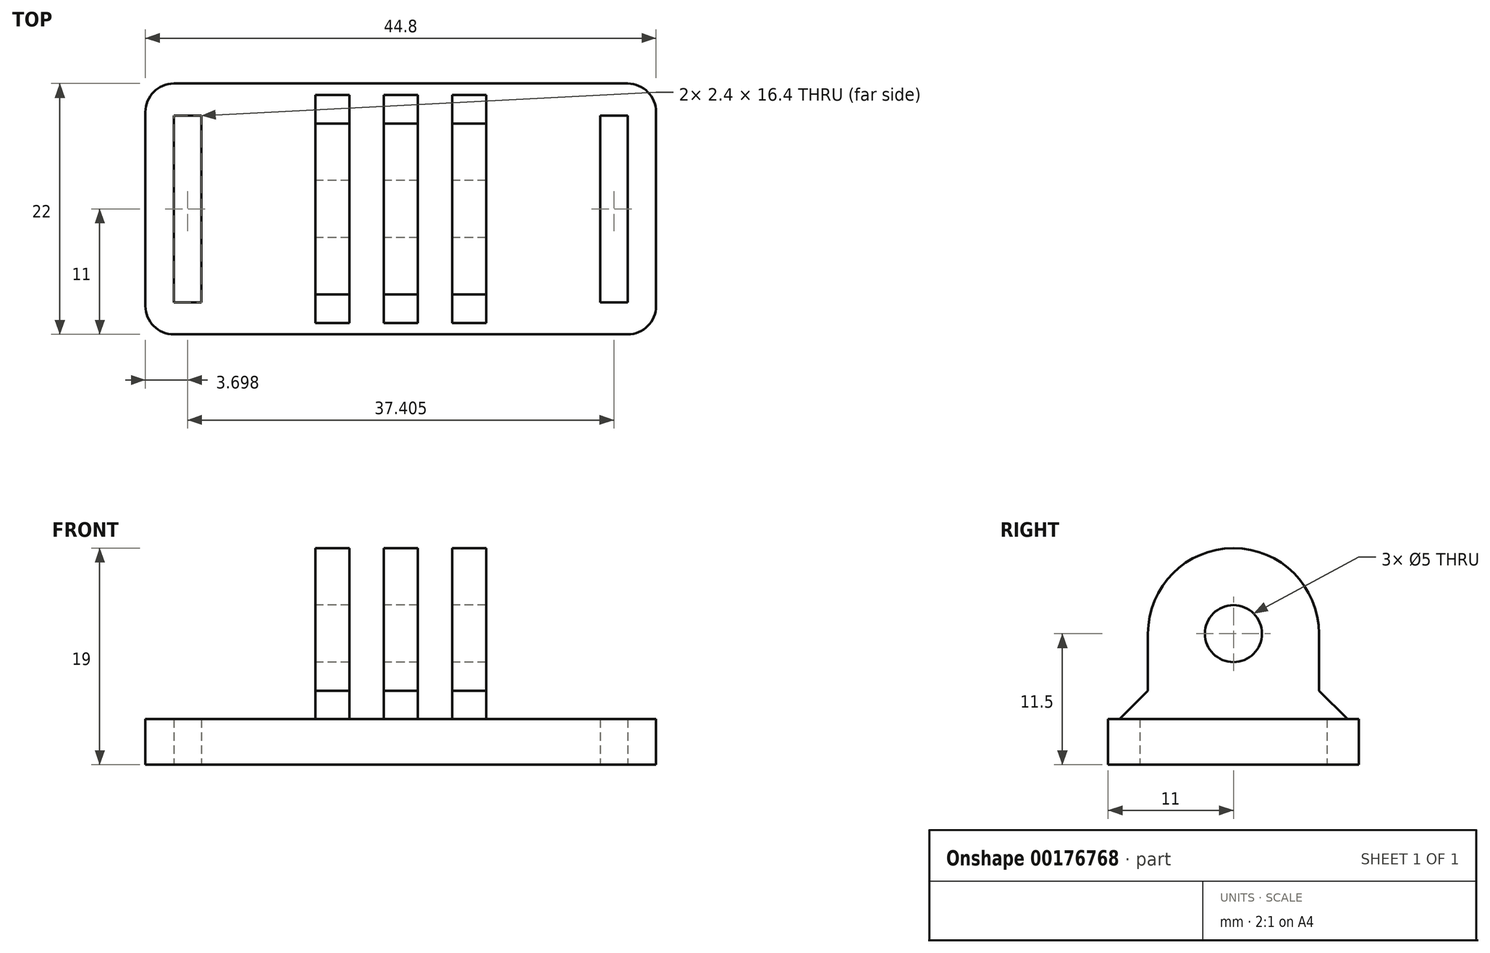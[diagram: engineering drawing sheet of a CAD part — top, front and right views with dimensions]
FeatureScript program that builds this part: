
annotation { "Feature Type Name" : "Feature", "Feature Type Description" : "" }
export const myFeature = defineFeature(function(context is Context, id is Id, definition is map)
    precondition{}
    {
        {
            var Q0;
            Q0=qCreatedBy(makeId("Top.planeOp"),FACE);
            var sketch = newSketch(context, id + "F0", { "sketchPlane" : qUnion([Q0])});
            skLineSegment(sketch, "E0.bottom", {"start": v(-22.4, 11) * mm, "end": v(22.4, 11) * mm});
            skLineSegment(sketch, "E0.top", {"start": v(-22.4, -11) * mm, "end": v(22.4, -11) * mm});
            skLineSegment(sketch, "E0.left", {"start": v(-22.4, 11) * mm, "end": v(-22.4, -11) * mm});
            skLineSegment(sketch, "E0.right", {"start": v(22.4, 11) * mm, "end": v(22.4, -11) * mm});
            skPoint(sketch, "E0.middle", {"position": v(0, 0) * mm});
            skLineSegment(sketch, "E1", {"start": v(5.64, 11) * mm, "end": v(0, 11) * mm});
            skLineSegment(sketch, "E2", {"start": v(0, 11) * mm, "end": v(-5.64, 11) * mm});
            skLineSegment(sketch, "E3.bottom", {"start": v(-7.5, 7.5) * mm, "end": v(-4.5, 7.5) * mm});
            skLineSegment(sketch, "E3.top", {"start": v(-7.5, -7.5) * mm, "end": v(-4.5, -7.5) * mm});
            skLineSegment(sketch, "E3.left", {"start": v(-7.5, 7.5) * mm, "end": v(-7.5, -7.5) * mm});
            skLineSegment(sketch, "E3.right", {"start": v(-4.5, 7.5) * mm, "end": v(-4.5, -7.5) * mm});
            skPoint(sketch, "E3.middle", {"position": v(-6, 0) * mm});
            skLineSegment(sketch, "E4.bottom", {"start": v(-1.5, 7.5) * mm, "end": v(1.5, 7.5) * mm});
            skLineSegment(sketch, "E4.top", {"start": v(-1.5, -7.5) * mm, "end": v(1.5, -7.5) * mm});
            skLineSegment(sketch, "E4.left", {"start": v(-1.5, 7.5) * mm, "end": v(-1.5, -7.5) * mm});
            skLineSegment(sketch, "E4.right", {"start": v(1.5, 7.5) * mm, "end": v(1.5, -7.5) * mm});
            skLineSegment(sketch, "E5.bottom", {"start": v(4.5, 7.5) * mm, "end": v(7.5, 7.5) * mm});
            skLineSegment(sketch, "E5.top", {"start": v(4.5, -7.5) * mm, "end": v(7.5, -7.5) * mm});
            skLineSegment(sketch, "E5.left", {"start": v(4.5, 7.5) * mm, "end": v(4.5, -7.5) * mm});
            skLineSegment(sketch, "E5.right", {"start": v(7.5, 7.5) * mm, "end": v(7.5, -7.5) * mm});
            skPoint(sketch, "E5.middle", {"position": v(6, 0) * mm});
            skLineSegment(sketch, "E6", {"start": v(-4.5, 7.5) * mm, "end": v(-1.5, 7.5) * mm});
            skLineSegment(sketch, "E7", {"start": v(4.5, 7.5) * mm, "end": v(1.5, 7.5) * mm});
            skLineSegment(sketch, "E8", {"start": v(-1.5, 0) * mm, "end": v(1.5, 0) * mm, "construction": true});
            skLineSegment(sketch, "E9", {"start": v(-6, 0) * mm, "end": v(0, 0) * mm});
            skLineSegment(sketch, "E10", {"start": v(6, 0) * mm, "end": v(0, 0) * mm});
            skLineSegment(sketch, "E11", {"start": v(0, 11) * mm, "end": v(0, 0) * mm});
            skLineSegment(sketch, "E12.bottom", {"start": v(-17.5, 8.2) * mm, "end": v(-19.9, 8.2) * mm});
            skLineSegment(sketch, "E12.top", {"start": v(-17.5, -8.2) * mm, "end": v(-19.9, -8.2) * mm});
            skLineSegment(sketch, "E12.left", {"start": v(-17.5, 8.2) * mm, "end": v(-17.5, -8.2) * mm});
            skLineSegment(sketch, "E12.right", {"start": v(-19.9, 8.2) * mm, "end": v(-19.9, -8.2) * mm});
            skPoint(sketch, "E12.middle", {"position": v(-18.7, 0) * mm});
            skLineSegment(sketch, "E13.MirrorCS", {"start": v(17.5, 8.2) * mm, "end": v(19.9, 8.2) * mm});
            skLineSegment(sketch, "E14.MirrorCS", {"start": v(19.9, 8.2) * mm, "end": v(19.9, -8.2) * mm});
            skLineSegment(sketch, "E15.MirrorCS", {"start": v(17.5, 8.2) * mm, "end": v(17.5, -8.2) * mm});
            skLineSegment(sketch, "E16.MirrorCS", {"start": v(17.5, -8.2) * mm, "end": v(19.9, -8.2) * mm});
            skSolve(sketch);
        }
        {
            var Q0;
            Q0=qSketchRegion(id+"F0",true);
            var Q1;
            {var subQ5=sQuery(id+"F0.wireOp",EDGE,"E3.top");Q1=makeQuery(id+"F0.imprint","IMPRINT",FACE,{"disambiguationData":[TD([[makeQuery(id+"F0.imprint","IMPRINT",EDGE,{"derivedFrom":subQ5}),1.0]])]});}
            var Q2;
            {var subQ5=sQuery(id+"F0.wireOp",EDGE,"E3.bottom");Q2=makeQuery(id+"F0.imprint","IMPRINT",FACE,{"disambiguationData":[TD([[makeQuery(id+"F0.imprint","IMPRINT",EDGE,{"derivedFrom":subQ5}),-1.0]])]});}
            var Q3;
            {var subQ5=sQuery(id+"F0.wireOp",EDGE,"E6");Q3=makeQuery(id+"F0.imprint","IMPRINT",FACE,{"disambiguationData":[TD([[makeQuery(id+"F0.imprint","IMPRINT",EDGE,{"derivedFrom":subQ5}),-1.0]])]});}
            var Q4;
            {var subQ1=sQuery(id+"F0.wireOp",EDGE,"E4.bottom");Q4=makeQuery(id+"F0.imprint","IMPRINT",FACE,{"disambiguationData":[TD([[makeQuery(id+"F0.imprint","IMPRINT",EDGE,{"derivedFrom":subQ1}),-1.0]])]});}
            var Q5;
            {var subQ0=sQuery(id+"F0.wireOp",EDGE,"E4.top");Q5=makeQuery(id+"F0.imprint","IMPRINT",FACE,{"disambiguationData":[TD([[makeQuery(id+"F0.imprint","IMPRINT",EDGE,{"derivedFrom":subQ0}),1.0]])]});}
            var Q6;
            {var subQ5=sQuery(id+"F0.wireOp",EDGE,"E7");Q6=makeQuery(id+"F0.imprint","IMPRINT",FACE,{"disambiguationData":[TD([[makeQuery(id+"F0.imprint","IMPRINT",EDGE,{"derivedFrom":subQ5}),1.0]])]});}
            var Q7;
            {var subQ5=sQuery(id+"F0.wireOp",EDGE,"E5.top");Q7=makeQuery(id+"F0.imprint","IMPRINT",FACE,{"disambiguationData":[TD([[makeQuery(id+"F0.imprint","IMPRINT",EDGE,{"derivedFrom":subQ5}),1.0]])]});}
            var Q8;
            {var subQ5=sQuery(id+"F0.wireOp",EDGE,"E5.bottom");Q8=makeQuery(id+"F0.imprint","IMPRINT",FACE,{"disambiguationData":[TD([[makeQuery(id+"F0.imprint","IMPRINT",EDGE,{"derivedFrom":subQ5}),-1.0]])]});}
            extrude(context, id + "F1", {"entities" : qUnion([Q0, Q1, Q2, Q3, Q4, Q5, Q6, Q7, Q8]), "depth" : 4 * mm});
        }
        {
            var Q0;
            {var subQ5=sQuery(id+"F0.wireOp",EDGE,"E3.top");Q0=makeQuery(id+"F0.imprint","IMPRINT",FACE,{"disambiguationData":[TD([[makeQuery(id+"F0.imprint","IMPRINT",EDGE,{"derivedFrom":subQ5}),1.0]])]});}
            var Q1;
            {var subQ5=sQuery(id+"F0.wireOp",EDGE,"E3.bottom");Q1=makeQuery(id+"F0.imprint","IMPRINT",FACE,{"disambiguationData":[TD([[makeQuery(id+"F0.imprint","IMPRINT",EDGE,{"derivedFrom":subQ5}),-1.0]])]});}
            var Q2;
            {var subQ1=sQuery(id+"F0.wireOp",EDGE,"E4.bottom");Q2=makeQuery(id+"F0.imprint","IMPRINT",FACE,{"disambiguationData":[TD([[makeQuery(id+"F0.imprint","IMPRINT",EDGE,{"derivedFrom":subQ1}),-1.0]])]});}
            var Q3;
            {var subQ0=sQuery(id+"F0.wireOp",EDGE,"E4.top");Q3=makeQuery(id+"F0.imprint","IMPRINT",FACE,{"disambiguationData":[TD([[makeQuery(id+"F0.imprint","IMPRINT",EDGE,{"derivedFrom":subQ0}),1.0]])]});}
            var Q4;
            {var subQ5=sQuery(id+"F0.wireOp",EDGE,"E5.top");Q4=makeQuery(id+"F0.imprint","IMPRINT",FACE,{"disambiguationData":[TD([[makeQuery(id+"F0.imprint","IMPRINT",EDGE,{"derivedFrom":subQ5}),1.0]])]});}
            var Q5;
            {var subQ5=sQuery(id+"F0.wireOp",EDGE,"E5.bottom");Q5=makeQuery(id+"F0.imprint","IMPRINT",FACE,{"disambiguationData":[TD([[makeQuery(id+"F0.imprint","IMPRINT",EDGE,{"derivedFrom":subQ5}),-1.0]])]});}
            extrude(context, id + "F2", {"entities" : qUnion([Q0, Q1, Q2, Q3, Q4, Q5]), "operationType" : NewBodyOperationType.ADD, "depth" : (15 + 4) * mm});
        }
        {
            var Q0;
            Q0=makeQuery(id+"F2.opExtrude","CAP_EDGE",EDGE,{"disambiguationData":[OSD([sQuery(id+"F0.wireOp",EDGE,"E3.top")])],"isStart":false});
            var Q1;
            Q1=makeQuery(id+"F2.opExtrude","CAP_EDGE",EDGE,{"disambiguationData":[OSD([sQuery(id+"F0.wireOp",EDGE,"E4.top")])],"isStart":false});
            var Q2;
            Q2=makeQuery(id+"F2.opExtrude","CAP_EDGE",EDGE,{"disambiguationData":[OSD([sQuery(id+"F0.wireOp",EDGE,"E5.top")])],"isStart":false});
            var Q3;
            Q3=makeQuery(id+"F2.opExtrude","CAP_EDGE",EDGE,{"disambiguationData":[OSD([sQuery(id+"F0.wireOp",EDGE,"E5.bottom")])],"isStart":false});
            var Q4;
            Q4=makeQuery(id+"F2.opExtrude","CAP_EDGE",EDGE,{"disambiguationData":[OSD([sQuery(id+"F0.wireOp",EDGE,"E4.bottom")])],"isStart":false});
            var Q5;
            Q5=makeQuery(id+"F2.opExtrude","CAP_EDGE",EDGE,{"disambiguationData":[OSD([sQuery(id+"F0.wireOp",EDGE,"E3.bottom")])],"isStart":false});
            fillet(context, id + "F3", {"entities" : qUnion([Q0, Q1, Q2, Q3, Q4, Q5]), "radius" : (15 / 2) * mm, "tangentPropagation" : true, "allowEdgeOverflow" : false});
        }
        {
            var Q0;
            Q0=makeQuery(id+"F2.opExtrude","SWEPT_FACE",FACE,{"disambiguationData":[OSD([sQuery(id+"F0.wireOp",EDGE,"E3.left")])]});
            var sketch = newSketch(context, id + "F4", { "sketchPlane" : qUnion([Q0])});
            skCircle(sketch, "E17", {"center": v(0, 11.5) * mm, "radius": 2.5 * mm});
            skSolve(sketch);
        }
        {
            var Q0;
            Q0=qSketchRegion(id+"F4",true);
            extrude(context, id + "F5", {"entities" : qUnion([Q0]), "operationType" : NewBodyOperationType.REMOVE, "endBound" : BoundingType.THROUGH_ALL, "oppositeDirection" : true, "depth" : 25 * mm});
        }
        {
            var Q0;
            Q0=makeQuery(id+"F2.boolean.opBoolean","INTERSECT",EDGE,{"derivedFrom":[makeQuery(id+"F1.opExtrude","CAP_FACE",FACE,{"disambiguationData":[OSD([sQuery(id+"F0.wireOp",EDGE,"E0.bottom"),sQuery(id+"F0.wireOp",EDGE,"E0.top"),sQuery(id+"F0.wireOp",EDGE,"E0.left"),sQuery(id+"F0.wireOp",EDGE,"E0.right"),sQuery(id+"F0.wireOp",EDGE,"E1"),sQuery(id+"F0.wireOp",EDGE,"E2")])],"isStart":false}),makeQuery(id+"F2.opExtrude","SWEPT_FACE",FACE,{"disambiguationData":[OSD([sQuery(id+"F0.wireOp",EDGE,"E3.bottom")])]})]});
            var Q1;
            Q1=makeQuery(id+"F2.boolean.opBoolean","INTERSECT",EDGE,{"derivedFrom":[makeQuery(id+"F1.opExtrude","CAP_FACE",FACE,{"disambiguationData":[OSD([sQuery(id+"F0.wireOp",EDGE,"E0.bottom"),sQuery(id+"F0.wireOp",EDGE,"E0.top"),sQuery(id+"F0.wireOp",EDGE,"E0.left"),sQuery(id+"F0.wireOp",EDGE,"E0.right"),sQuery(id+"F0.wireOp",EDGE,"E1"),sQuery(id+"F0.wireOp",EDGE,"E2")])],"isStart":false}),makeQuery(id+"F2.opExtrude","SWEPT_FACE",FACE,{"disambiguationData":[OSD([sQuery(id+"F0.wireOp",EDGE,"E4.bottom")])]})]});
            var Q2;
            Q2=makeQuery(id+"F2.boolean.opBoolean","INTERSECT",EDGE,{"derivedFrom":[makeQuery(id+"F1.opExtrude","CAP_FACE",FACE,{"disambiguationData":[OSD([sQuery(id+"F0.wireOp",EDGE,"E0.bottom"),sQuery(id+"F0.wireOp",EDGE,"E0.top"),sQuery(id+"F0.wireOp",EDGE,"E0.left"),sQuery(id+"F0.wireOp",EDGE,"E0.right"),sQuery(id+"F0.wireOp",EDGE,"E1"),sQuery(id+"F0.wireOp",EDGE,"E2")])],"isStart":false}),makeQuery(id+"F2.opExtrude","SWEPT_FACE",FACE,{"disambiguationData":[OSD([sQuery(id+"F0.wireOp",EDGE,"E5.bottom")])]})]});
            var Q3;
            Q3=makeQuery(id+"F2.boolean.opBoolean","INTERSECT",EDGE,{"derivedFrom":[makeQuery(id+"F1.opExtrude","CAP_FACE",FACE,{"disambiguationData":[OSD([sQuery(id+"F0.wireOp",EDGE,"E0.bottom"),sQuery(id+"F0.wireOp",EDGE,"E0.top"),sQuery(id+"F0.wireOp",EDGE,"E0.left"),sQuery(id+"F0.wireOp",EDGE,"E0.right"),sQuery(id+"F0.wireOp",EDGE,"E1"),sQuery(id+"F0.wireOp",EDGE,"E2")])],"isStart":false}),makeQuery(id+"F2.opExtrude","SWEPT_FACE",FACE,{"disambiguationData":[OSD([sQuery(id+"F0.wireOp",EDGE,"E3.top")])]})]});
            var Q4;
            Q4=makeQuery(id+"F2.boolean.opBoolean","INTERSECT",EDGE,{"derivedFrom":[makeQuery(id+"F1.opExtrude","CAP_FACE",FACE,{"disambiguationData":[OSD([sQuery(id+"F0.wireOp",EDGE,"E0.bottom"),sQuery(id+"F0.wireOp",EDGE,"E0.top"),sQuery(id+"F0.wireOp",EDGE,"E0.left"),sQuery(id+"F0.wireOp",EDGE,"E0.right"),sQuery(id+"F0.wireOp",EDGE,"E1"),sQuery(id+"F0.wireOp",EDGE,"E2")])],"isStart":false}),makeQuery(id+"F2.opExtrude","SWEPT_FACE",FACE,{"disambiguationData":[OSD([sQuery(id+"F0.wireOp",EDGE,"E4.top")])]})]});
            var Q5;
            Q5=makeQuery(id+"F2.boolean.opBoolean","INTERSECT",EDGE,{"derivedFrom":[makeQuery(id+"F1.opExtrude","CAP_FACE",FACE,{"disambiguationData":[OSD([sQuery(id+"F0.wireOp",EDGE,"E0.bottom"),sQuery(id+"F0.wireOp",EDGE,"E0.top"),sQuery(id+"F0.wireOp",EDGE,"E0.left"),sQuery(id+"F0.wireOp",EDGE,"E0.right"),sQuery(id+"F0.wireOp",EDGE,"E1"),sQuery(id+"F0.wireOp",EDGE,"E2")])],"isStart":false}),makeQuery(id+"F2.opExtrude","SWEPT_FACE",FACE,{"disambiguationData":[OSD([sQuery(id+"F0.wireOp",EDGE,"E5.top")])]})]});
            chamfer(context, id + "F6", {"entities" : qUnion([Q0, Q1, Q2, Q3, Q4, Q5]), "width" : 2.5 * mm, "tangentPropagation" : true});
        }
        {
            var Q0;
            Q0=makeQuery(id+"F1.opExtrude","SWEPT_EDGE",EDGE,{"disambiguationData":[OSD([sQuery(id+"F0.wireOp",EDGE,"CLPGVFCl-r30g-CXwn-TlbT-r3UxW4kqERAr"),sQuery(id+"F0.wireOp",EDGE,"oR9epeVS-WqLV-4rL8-s4B5-AoyoQnr77yQD")])]});
            var Q1;
            Q1=makeQuery(id+"F1.opExtrude","SWEPT_EDGE",EDGE,{"disambiguationData":[OSD([sQuery(id+"F0.wireOp",EDGE,"DJ114h8q-qToH-2vKu-dRtU-9KACn9xQiOdX"),sQuery(id+"F0.wireOp",EDGE,"CLPGVFCl-r30g-CXwn-TlbT-r3UxW4kqERAr")])]});
            var Q2;
            Q2=makeQuery(id+"F1.opExtrude","SWEPT_EDGE",EDGE,{"disambiguationData":[OSD([sQuery(id+"F0.wireOp",EDGE,"E0.bottom"),sQuery(id+"F0.wireOp",EDGE,"E0.left")])]});
            var Q3;
            Q3=makeQuery(id+"F1.opExtrude","SWEPT_EDGE",EDGE,{"disambiguationData":[OSD([sQuery(id+"F0.wireOp",EDGE,"E0.top"),sQuery(id+"F0.wireOp",EDGE,"E0.left")])]});
            var Q4;
            Q4=makeQuery(id+"F1.opExtrude","SWEPT_EDGE",EDGE,{"disambiguationData":[OSD([sQuery(id+"F0.wireOp",EDGE,"E0.top"),sQuery(id+"F0.wireOp",EDGE,"E0.right")])]});
            var Q5;
            Q5=makeQuery(id+"F1.opExtrude","SWEPT_EDGE",EDGE,{"disambiguationData":[OSD([sQuery(id+"F0.wireOp",EDGE,"E0.bottom"),sQuery(id+"F0.wireOp",EDGE,"E0.right")])]});
            fillet(context, id + "F7", {"entities" : qUnion([Q0, Q1, Q2, Q3, Q4, Q5]), "radius" : 2.5 * mm, "tangentPropagation" : true, "allowEdgeOverflow" : false});
        }
    });
